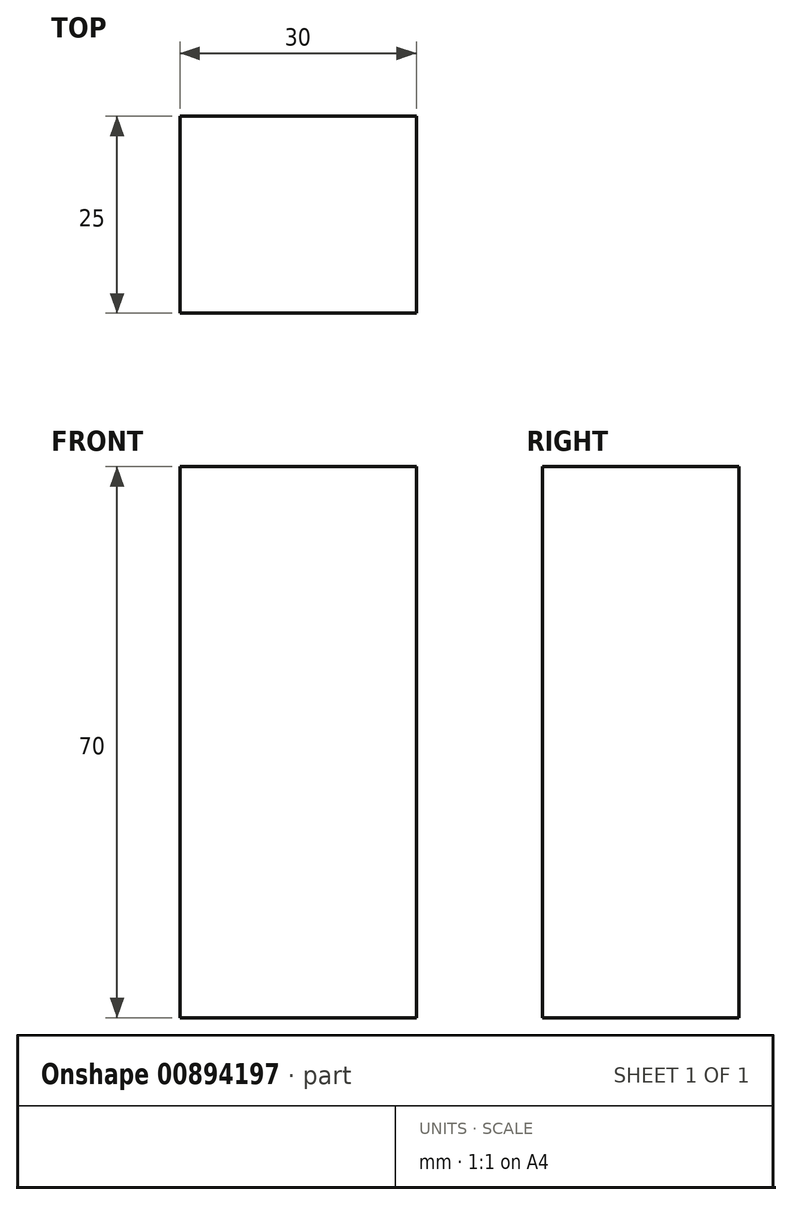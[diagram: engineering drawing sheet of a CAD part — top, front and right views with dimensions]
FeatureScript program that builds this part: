
annotation { "Feature Type Name" : "Feature", "Feature Type Description" : "" }
export const myFeature = defineFeature(function(context is Context, id is Id, definition is map)
    precondition{}
    {
        {
            var Q0;
            Q0=qCreatedBy(makeId("Front.planeOp"),FACE);
            var sketch = newSketch(context, id + "F0", { "sketchPlane" : qUnion([Q0])});
            skLineSegment(sketch, "E0", {"start": v(-23.93, 0) * mm, "end": v(-23.93, 70) * mm});
            skLineSegment(sketch, "E1", {"start": v(6.07, 0) * mm, "end": v(6.07, 70) * mm});
            skLineSegment(sketch, "E2", {"start": v(-23.93, 70) * mm, "end": v(6.07, 70) * mm});
            skLineSegment(sketch, "E3", {"start": v(6.07, 0) * mm, "end": v(-23.93, 0) * mm});
            skSolve(sketch);
        }
        {
            var Q0;
            Q0 = qSketchRegion(id + "F0", true);
            extrude(context, id + "F1", {"entities" : qUnion([Q0]), "endBound" : BoundingType.SYMMETRIC, "depth" : 25 * mm, "offsetDistance" : 25 * mm});
        }
    });
